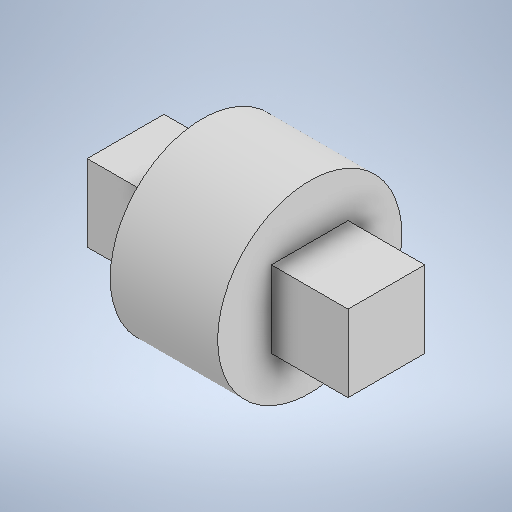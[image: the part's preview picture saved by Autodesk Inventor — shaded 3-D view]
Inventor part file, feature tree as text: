
AUTODESK INVENTOR PART (.ipt)
format: ipt  version: 2025.1 (Build 291241000, 241)  size: 241,664 bytes
history: native  units: mm
features: sketch x2, revolve x1, plane x1, extrude x1
ambient origin geometry x8: Origin, YZ Plane, XZ Plane, XY Plane, X Axis, Y Axis, Z Axis, Center Point
bodies: Solid1 (feature_tree)
feature tree (5):
  revolve  "Revolution1"  [1 undecoded]
  plane  "Work Plane1"
  extrude  "Extrusion1"  Depth=5.0mm
  sketch  "Sketch1"  dims[d0=12.0mm d1=7.0mm]
  sketch  "Sketch2"  dims[d2=90.0deg d3=5.0mm d4=5.0mm d5=17.0mm d6=0.0mm]
note: 1 required parameter value undecoded (feature->parameter linkage not recoverable at this tier; creation-order binding heuristic only, values carry confidence <= 0.55)
